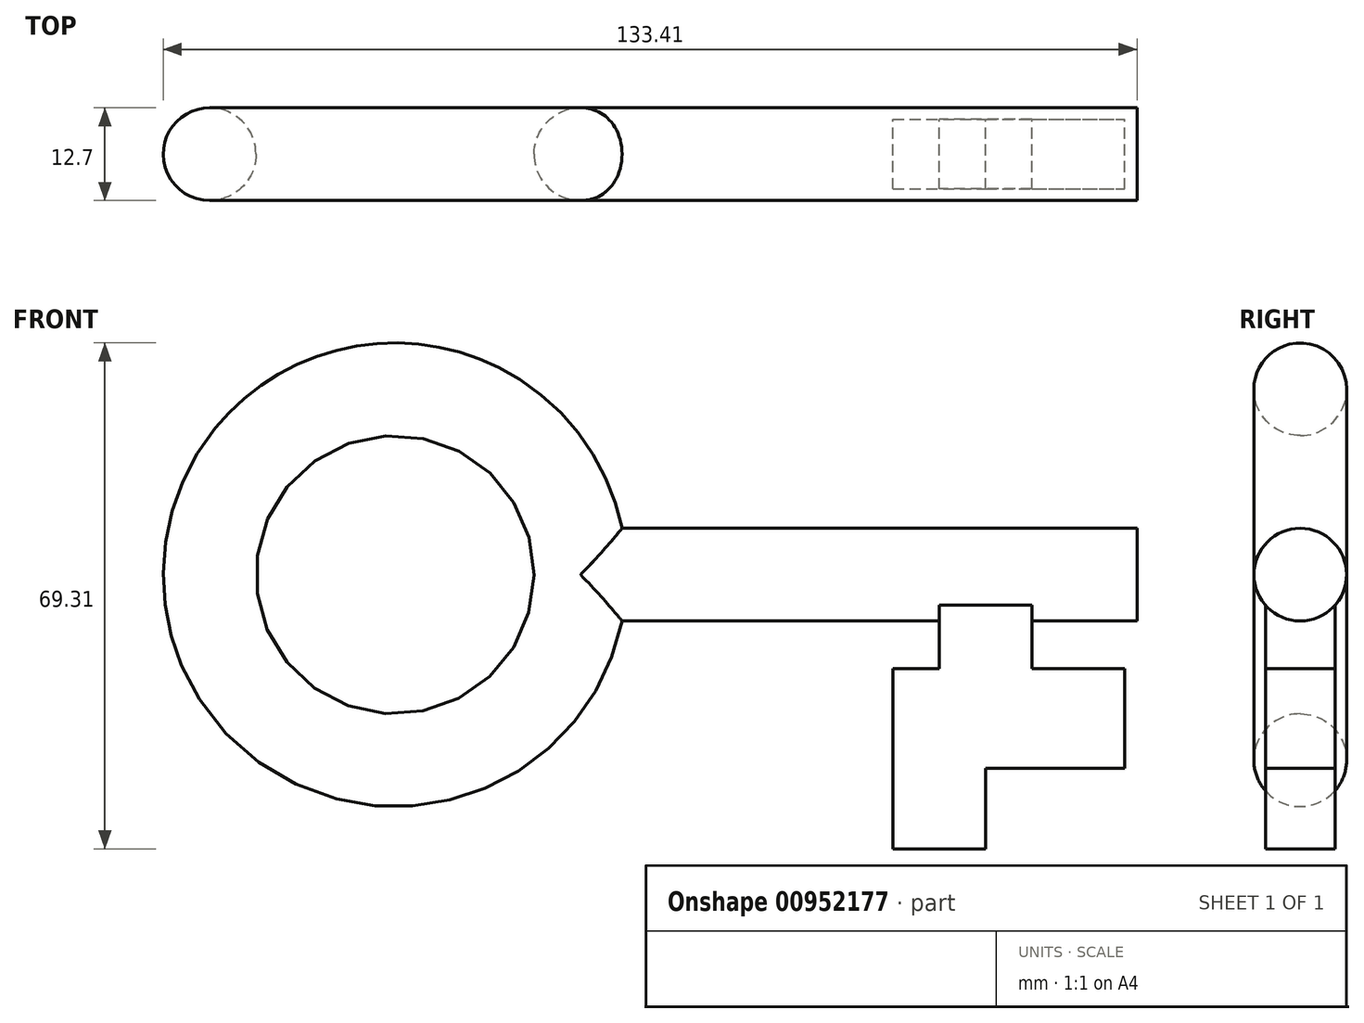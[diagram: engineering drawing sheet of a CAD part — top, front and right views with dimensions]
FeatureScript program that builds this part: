
annotation { "Feature Type Name" : "Feature", "Feature Type Description" : "" }
export const myFeature = defineFeature(function(context is Context, id is Id, definition is map)
    precondition{}
    {
        {
            var Q0;
            Q0=qCreatedBy(makeId("Front.planeOp"),FACE);
            var sketch = newSketch(context, id + "F0", { "sketchPlane" : qUnion([Q0])});
            skCircle(sketch, "E0", {"center": v(0, 0) * mm, "radius": 31.75 * mm});
            skCircle(sketch, "E1", {"center": v(0, 0) * mm, "radius": 19.05 * mm});
            skPoint(sketch, "E2.middle", {"position": v(77.71, 0) * mm});
            skSolve(sketch);
        }
        {
            var Q0;
            Q0=makeQuery(id+"F0.imprint","IMPRINT",FACE,{"disambiguationData":[TD([[makeQuery(id+"F0.imprint","IMPRINT",EDGE,{"derivedFrom":sQuery(id+"F0.wireOp",EDGE,"E0")}),1.0]])]});
            extrude(context, id + "F1", {"entities" : qUnion([Q0]), "endBound" : BoundingType.SYMMETRIC, "depth" : 12.7 * mm, "offsetDistance" : 25.4 * mm});
        }
        {
            var Q0;
            Q0=makeQuery(id+"F1.opExtrude","CAP_EDGE",EDGE,{"disambiguationData":[OSD([sQuery(id+"F0.wireOp",EDGE,"E0")])],"isStart":false});
            var Q1;
            Q1=makeQuery(id+"F1.opExtrude","CAP_EDGE",EDGE,{"disambiguationData":[OSD([sQuery(id+"F0.wireOp",EDGE,"E0")])],"isStart":true});
            fillet(context, id + "F2", {"entities" : qUnion([Q0, Q1]), "radius" : 6.35 * mm, "tangentPropagation" : true, "allowEdgeOverflow" : false});
        }
        {
            var Q0;
            Q0=makeQuery(id+"F1.opExtrude","CAP_EDGE",EDGE,{"disambiguationData":[OSD([sQuery(id+"F0.wireOp",EDGE,"E1")])],"isStart":false});
            var Q1;
            Q1=makeQuery(id+"F1.opExtrude","CAP_EDGE",EDGE,{"disambiguationData":[OSD([sQuery(id+"F0.wireOp",EDGE,"E1")])],"isStart":true});
            fillet(context, id + "F3", {"entities" : qUnion([Q0, Q1]), "radius" : 6.35 * mm, "tangentPropagation" : true, "allowEdgeOverflow" : false});
        }
        {
            var Q0;
            Q0=qCreatedBy(makeId("Front.planeOp"),FACE);
            var sketch = newSketch(context, id + "F4", { "sketchPlane" : qUnion([Q0])});
            skLineSegment(sketch, "E3.left", {"start": v(0, 0) * mm, "end": v(0, 0) * mm});
            skLineSegment(sketch, "E4.bottom", {"start": v(25.46, 0) * mm, "end": v(101.66, 0) * mm});
            skLineSegment(sketch, "E4.top", {"start": v(25.46, 6.35) * mm, "end": v(101.66, 6.35) * mm});
            skLineSegment(sketch, "E4.left", {"start": v(25.46, 0) * mm, "end": v(25.46, 6.35) * mm});
            skLineSegment(sketch, "E4.right", {"start": v(101.66, 0) * mm, "end": v(101.66, 6.35) * mm});
            skSolve(sketch);
        }
        {
            var Q0;
            Q0=makeQuery(id+"F4.imprint","IMPRINT",FACE,{"disambiguationData":[TD([[makeQuery(id+"F4.imprint","IMPRINT",EDGE,{"derivedFrom":sQuery(id+"F4.wireOp",EDGE,"E4.bottom")}),1.0]])]});
            var Q1;
            Q1=sQuery(id+"F4.wireOp",EDGE,"E4.bottom");
            revolve(context, id + "F5", {"operationType" : NewBodyOperationType.ADD, "surfaceOperationType" : NewSurfaceOperationType.NEW, "entities" : qUnion([Q0]), "axis" : qUnion([Q1]), "revolveType" : RevolveType.FULL});
        }
        {
            var Q0;
            Q0=qCreatedBy(makeId("Front.planeOp"),FACE);
            var sketch = newSketch(context, id + "F6", { "sketchPlane" : qUnion([Q0])});
            skLineSegment(sketch, "E5.bottom", {"start": v(74.57, -0.18) * mm, "end": v(87.27, -0.18) * mm});
            skLineSegment(sketch, "E5.top", {"start": v(74.57, -12.88) * mm, "end": v(87.27, -12.88) * mm});
            skLineSegment(sketch, "E5.left", {"start": v(74.57, -0.18) * mm, "end": v(74.57, -12.88) * mm});
            skLineSegment(sketch, "E5.right", {"start": v(87.27, -0.18) * mm, "end": v(87.27, -12.88) * mm});
            skLineSegment(sketch, "E6.bottom", {"start": v(68.22, -12.88) * mm, "end": v(99.97, -12.88) * mm});
            skLineSegment(sketch, "E6.top", {"start": v(68.22, -26.5) * mm, "end": v(99.97, -26.5) * mm});
            skLineSegment(sketch, "E6.left", {"start": v(68.22, -12.88) * mm, "end": v(68.22, -26.5) * mm});
            skLineSegment(sketch, "E6.right", {"start": v(99.97, -12.88) * mm, "end": v(99.97, -26.5) * mm});
            skLineSegment(sketch, "E7.bottom", {"start": v(68.22, -26.5) * mm, "end": v(74.57, -26.5) * mm});
            skLineSegment(sketch, "E8.bottom", {"start": v(99.97, -26.5) * mm, "end": v(87.27, -26.5) * mm});
            skLineSegment(sketch, "E8.top", {"start": v(99.97, -37.47) * mm, "end": v(87.27, -37.47) * mm});
            skLineSegment(sketch, "E8.left", {"start": v(99.97, -26.5) * mm, "end": v(99.97, -37.47) * mm});
            skLineSegment(sketch, "E8.right", {"start": v(87.27, -26.5) * mm, "end": v(87.27, -37.47) * mm});
            skLineSegment(sketch, "E9.bottom", {"start": v(68.22, -26.5) * mm, "end": v(80.92, -26.5) * mm});
            skLineSegment(sketch, "E9.top", {"start": v(68.22, -37.56) * mm, "end": v(80.92, -37.56) * mm});
            skLineSegment(sketch, "E9.left", {"start": v(68.22, -26.5) * mm, "end": v(68.22, -37.56) * mm});
            skLineSegment(sketch, "E9.right", {"start": v(80.92, -26.5) * mm, "end": v(80.92, -37.56) * mm});
            skSolve(sketch);
        }
        {
            var Q0;
            Q0=makeQuery(id+"F6.imprint","IMPRINT",FACE,{"disambiguationData":[TD([[makeQuery(id+"F6.imprint","IMPRINT",EDGE,{"derivedFrom":sQuery(id+"F6.wireOp",EDGE,"E5.bottom")}),-1.0]])]});
            var Q1;
            {var subQ0=sQuery(id+"F6.wireOp",EDGE,"E6.top");Q1=makeQuery(id+"F6.imprint","IMPRINT",FACE,{"disambiguationData":[TD([[makeQuery(id+"F6.imprint","IMPRINT",EDGE,{"derivedFrom":subQ0}),1.0]])]});}
            var Q2;
            Q2=makeQuery(id+"F6.imprint","IMPRINT",FACE,{"disambiguationData":[TD([[makeQuery(id+"F6.imprint","IMPRINT",EDGE,{"derivedFrom":sQuery(id+"F6.wireOp",EDGE,"E9.top")}),1.0]])]});
            var Q3;
            Q3=makeQuery(id+"F6.imprint","IMPRINT",FACE,{"disambiguationData":[TD([[makeQuery(id+"F6.imprint","IMPRINT",EDGE,{"derivedFrom":sQuery(id+"F6.wireOp",EDGE,"E8.bottom")}),1.0]])]});
            extrude(context, id + "F7", {"entities" : qUnion([Q0, Q1, Q2, Q3]), "operationType" : NewBodyOperationType.ADD, "endBound" : BoundingType.SYMMETRIC, "depth" : 9.52 * mm, "offsetDistance" : 25.4 * mm});
        }
    });
